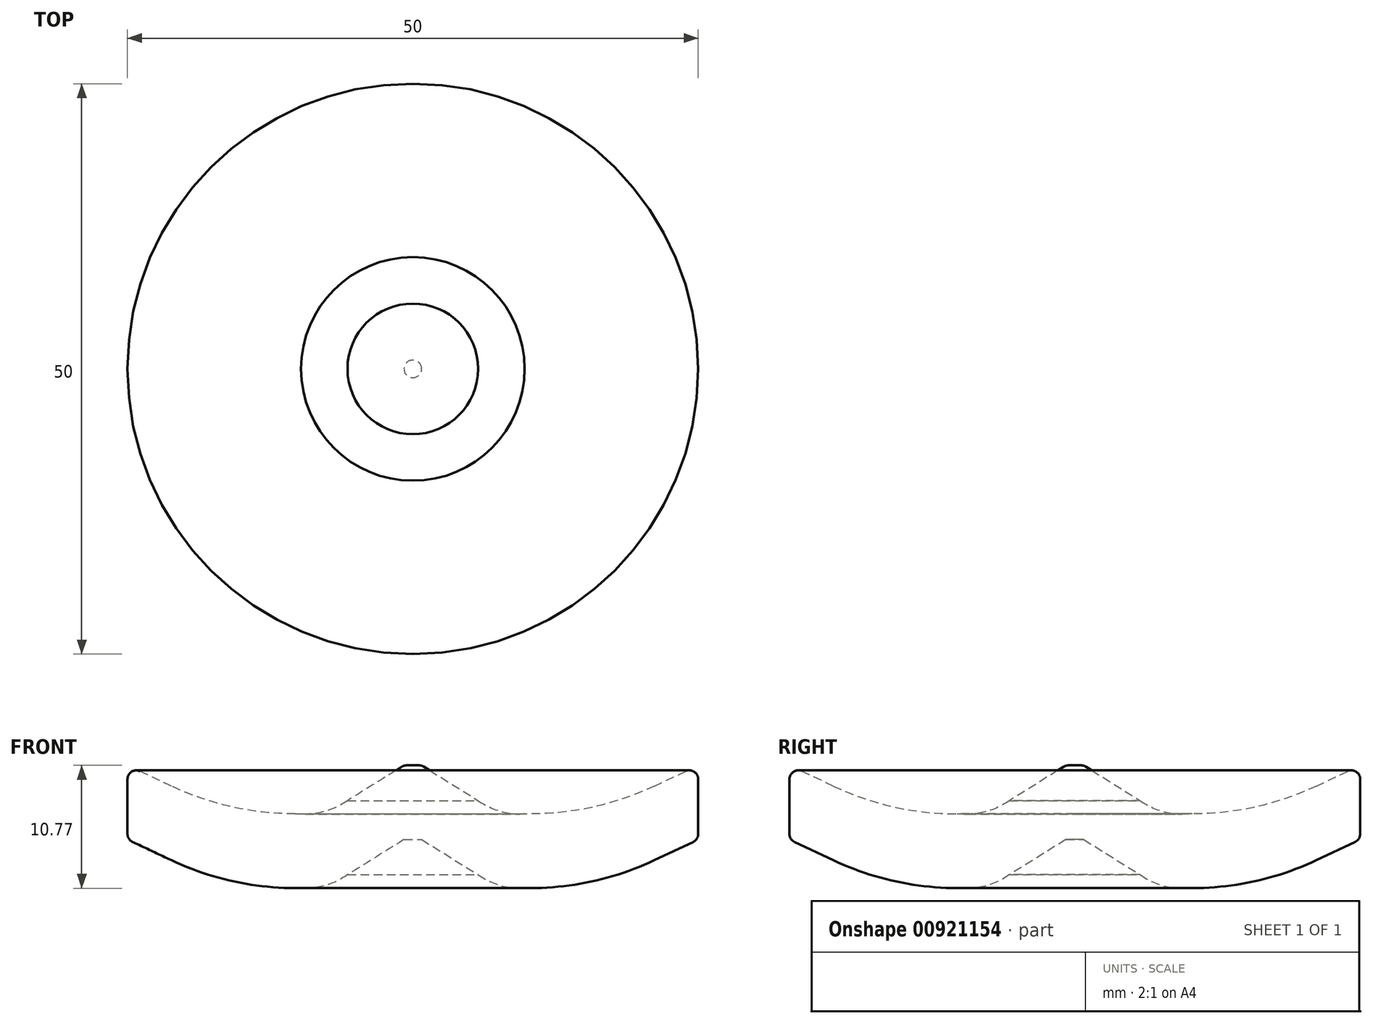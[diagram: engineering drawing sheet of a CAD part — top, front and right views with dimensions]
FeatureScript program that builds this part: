
annotation { "Feature Type Name" : "Feature", "Feature Type Description" : "" }
export const myFeature = defineFeature(function(context is Context, id is Id, definition is map)
    precondition{}
    {
        {
            var Q0;
            Q0=qCreatedBy(makeId("Front.planeOp"),FACE);
            var sketch = newSketch(context, id + "F0", { "sketchPlane" : qUnion([Q0])});
            skLineSegment(sketch, "E0", {"start": v(-21.15, 2.28) * mm, "end": v(-25, 4.1) * mm});
            skLineSegment(sketch, "E1", {"start": v(-5.72, 1.01) * mm, "end": v(-0.77, 4.1) * mm});
            skLineSegment(sketch, "E2", {"start": v(-0.77, 4.1) * mm, "end": v(0, 4.1) * mm});
            skLineSegment(sketch, "E3", {"start": v(-10.3, -0.15) * mm, "end": v(-9.8, -0.15) * mm});
            skPoint(sketch, "E4.visualSharp", {"position": v(-16, -0.15) * mm});
            skPoint(sketch, "E5.visualSharp", {"position": v(-7.6, -0.15) * mm});
            skArc(sketch, "E5.filletArc", {"start": v(-9.8, -0.15) * mm, "mid": v(-7.66, 0.08) * mm, "end": v(-5.72, 1.01) * mm});
            skArc(sketch, "E6.filletArc", {"start": v(-21.15, 2.28) * mm, "mid": v(-15.86, 0.46) * mm, "end": v(-10.3, -0.15) * mm});
            skLineSegment(sketch, "E7", {"start": v(-21.15, 8.78) * mm, "end": v(-25, 10.6) * mm});
            skLineSegment(sketch, "E8", {"start": v(-5.72, 7.51) * mm, "end": v(-0.77, 10.6) * mm});
            skLineSegment(sketch, "E9", {"start": v(-0.77, 10.6) * mm, "end": v(0, 10.6) * mm});
            skLineSegment(sketch, "E10", {"start": v(-10.3, 6.35) * mm, "end": v(-9.8, 6.35) * mm});
            skArc(sketch, "E11.filletArc", {"start": v(-9.8, 6.35) * mm, "mid": v(-7.66, 6.58) * mm, "end": v(-5.72, 7.51) * mm});
            skArc(sketch, "E12.filletArc", {"start": v(-21.15, 8.78) * mm, "mid": v(-15.86, 6.96) * mm, "end": v(-10.3, 6.35) * mm});
            skLineSegment(sketch, "E13", {"start": v(-25, 10.6) * mm, "end": v(-25, 4.1) * mm});
            skLineSegment(sketch, "E14", {"start": v(0, 10.6) * mm, "end": v(0, 4.1) * mm});
            skSolve(sketch);
        }
        {
            var Q0;
            Q0=qCreatedBy(makeId("Top.planeOp"),FACE);
            var sketch = newSketch(context, id + "F1", { "sketchPlane" : qUnion([Q0])});
            skCircle(sketch, "E15", {"center": v(0, 0) * mm, "radius": 17.04 * mm});
            skSolve(sketch);
        }
        {
            var Q0;
            Q0=makeQuery(id+"F0.imprint","IMPRINT",FACE,{"disambiguationData":[TD([[makeQuery(id+"F0.imprint","IMPRINT",EDGE,{"derivedFrom":sQuery(id+"F0.wireOp",EDGE,"E0")}),-1.0]])]});
            var Q1;
            Q1=sQuery(id+"F1.wireOp",EDGE,"E15");
            sweep(context, id + "F2", {"profiles" : qUnion([Q0]), "path" : qUnion([Q1])});
        }
        {
            var Q0;
            Q0=makeQuery(id+"F2.opSweep","SWEPT_EDGE",EDGE,{"disambiguationData":[OSD([sQuery(id+"F0.wireOp",EDGE,"E7"),sQuery(id+"F0.wireOp",EDGE,"E13"),sQuery(id+"F1.wireOp",EDGE,"E15")])]});
            var Q1;
            Q1=makeQuery(id+"F2.opSweep","SWEPT_EDGE",EDGE,{"disambiguationData":[OSD([sQuery(id+"F0.wireOp",EDGE,"E0"),sQuery(id+"F0.wireOp",EDGE,"E13"),sQuery(id+"F1.wireOp",EDGE,"E15")])]});
            var Q2;
            Q2=makeQuery(id+"F2.opSweep","SWEPT_EDGE",EDGE,{"disambiguationData":[OSD([sQuery(id+"F0.wireOp",EDGE,"E8"),sQuery(id+"F0.wireOp",EDGE,"E9"),sQuery(id+"F1.wireOp",EDGE,"E15")])]});
            fillet(context, id + "F3", {"entities" : qUnion([Q0, Q1, Q2]), "radius" : 0.76 * mm, "tangentPropagation" : true, "allowEdgeOverflow" : false});
        }
    });
